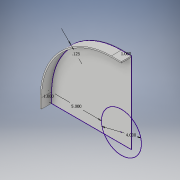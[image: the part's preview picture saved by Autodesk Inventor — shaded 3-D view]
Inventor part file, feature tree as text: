
AUTODESK INVENTOR PART (.ipt)
format: ipt  version: 2019 (Build 230136000, 136)  size: 121,344 bytes
history: native  units: in
note: dims shown in document units (in); Inventor stores cm internally (conversion verified against a paired STEP export)
features: extrude x2, sketch x1
ambient origin geometry x8: Origin, YZ Plane, XZ Plane, XY Plane, X Axis, Y Axis, Z Axis, Center Point
bodies: Solid1 (feature_tree)
feature tree (3):
  sketch  "Sketch1"  dims[d0=4.0in d1=5.0in d2=1.0in d3=1.0in d4=0.125in d5=1.0in d6=0.0in d7=0.06in d8=0.0in]
  extrude  "Extrusion1"  Depth=0.06in
  extrude  "Extrusion2"  Depth=1.0in
